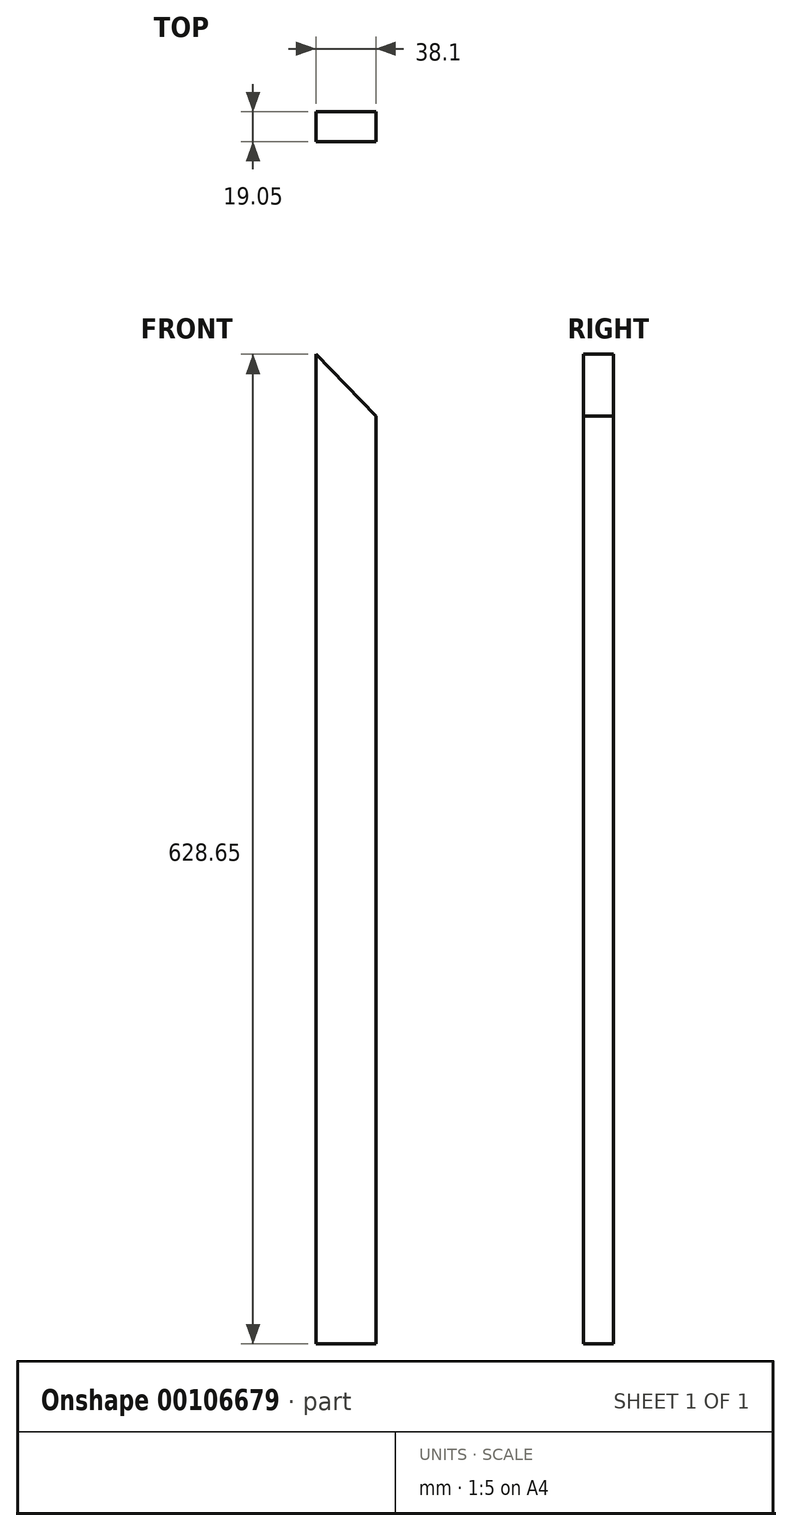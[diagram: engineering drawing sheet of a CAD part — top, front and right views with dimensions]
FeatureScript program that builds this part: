
annotation { "Feature Type Name" : "Feature", "Feature Type Description" : "" }
export const myFeature = defineFeature(function(context is Context, id is Id, definition is map)
    precondition{}
    {
        {
            var Q0;
            Q0=qCreatedBy(makeId("Front.planeOp"),FACE);
            var sketch = newSketch(context, id + "F0", { "sketchPlane" : qUnion([Q0])});
            skLineSegment(sketch, "E0.bottom", {"start": v(0, 0) * mm, "end": v(38.1, 0) * mm});
            skLineSegment(sketch, "E0.left", {"start": v(0, 0) * mm, "end": v(0, 628.65) * mm});
            skLineSegment(sketch, "E0.right", {"start": v(38.1, 0) * mm, "end": v(38.1, 589.32) * mm});
            skLineSegment(sketch, "E1", {"start": v(0, 628.65) * mm, "end": v(38.1, 589.32) * mm});
            skSolve(sketch);
        }
        {
            var Q0;
            Q0=makeQuery(id+"F0.imprint","IMPRINT",FACE,{"disambiguationData":[TD([[makeQuery(id+"F0.imprint","IMPRINT",EDGE,{"derivedFrom":sQuery(id+"F0.wireOp",EDGE,"E0.bottom")}),1.0]])]});
            extrude(context, id + "F1", {"entities" : qUnion([Q0]), "depth" : 19.05 * mm});
        }
    });
